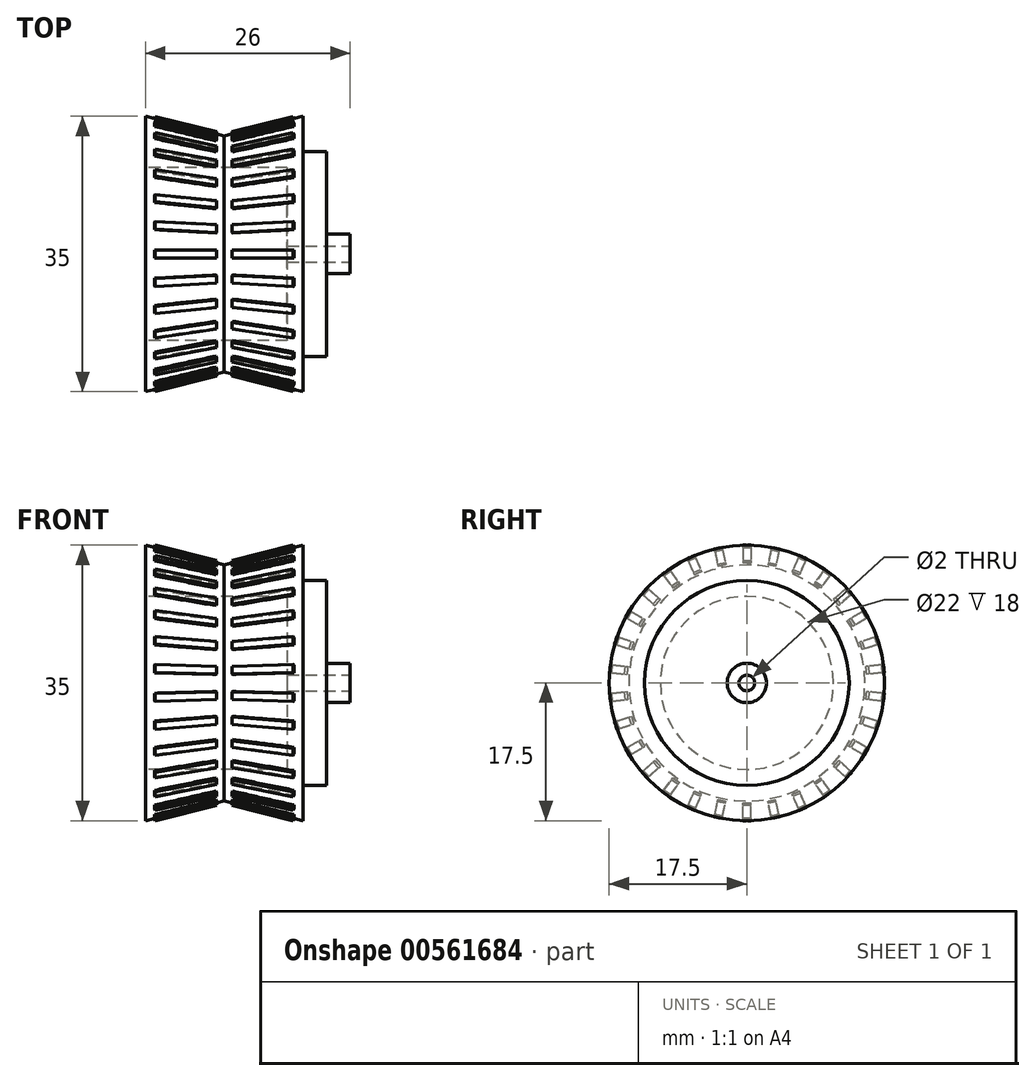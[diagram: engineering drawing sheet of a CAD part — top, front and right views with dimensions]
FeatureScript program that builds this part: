
annotation { "Feature Type Name" : "Feature", "Feature Type Description" : "" }
export const myFeature = defineFeature(function(context is Context, id is Id, definition is map)
    precondition{}
    {
        {
            var Q0;
            Q0=qCreatedBy(makeId("Front.planeOp"),FACE);
            var sketch = newSketch(context, id + "F0", { "sketchPlane" : qUnion([Q0])});
            skLineSegment(sketch, "E0", {"start": v(0, 15) * mm, "end": v(0, -15) * mm, "construction": true});
            skLineSegment(sketch, "E1", {"start": v(0, 15) * mm, "end": v(10, 17.5) * mm});
            skLineSegment(sketch, "E2", {"start": v(10, 17.5) * mm, "end": v(10, 0) * mm});
            skLineSegment(sketch, "E3", {"start": v(-10, 0) * mm, "end": v(-10, 17.5) * mm});
            skLineSegment(sketch, "E4", {"start": v(-10, 17.5) * mm, "end": v(0, 15) * mm});
            skLineSegment(sketch, "E5", {"start": v(-10, 0) * mm, "end": v(10, 0) * mm});
            skPoint(sketch, "E6.orphan", {"position": v(10, -17.5) * mm});
            skPoint(sketch, "E7.orphan", {"position": v(-10, -17.5) * mm});
            skSolve(sketch);
        }
        {
            var Q0;
            Q0=makeQuery(id+"F0.imprint","IMPRINT",FACE,{"disambiguationData":[TD([[makeQuery(id+"F0.imprint","IMPRINT",EDGE,{"derivedFrom":sQuery(id+"F0.wireOp",EDGE,"E1")}),-1.0]])]});
            var Q1;
            Q1=sQuery(id+"F0.wireOp",EDGE,"E5");
            revolve(context, id + "F1", {"entities" : qUnion([Q0]), "axis" : qUnion([Q1]), "revolveType" : RevolveType.FULL});
        }
        {
            var Q0;
            Q0=makeQuery(id+"F1.opRevolve","SWEPT_FACE",FACE,{"disambiguationData":[OSD([sQuery(id+"F0.wireOp",EDGE,"E2")])]});
            var sketch = newSketch(context, id + "F2", { "sketchPlane" : qUnion([Q0])});
            skCircle(sketch, "E8", {"center": v(0, 0) * mm, "radius": 13 * mm});
            skSolve(sketch);
        }
        {
            var Q0;
            Q0=makeQuery(id+"F2.imprint","IMPRINT",FACE,{"disambiguationData":[TD([[makeQuery(id+"F2.imprint","IMPRINT",EDGE,{"derivedFrom":sQuery(id+"F2.wireOp",EDGE,"E8")}),1.0]])]});
            extrude(context, id + "F3", {"entities" : qUnion([Q0]), "operationType" : NewBodyOperationType.ADD, "depth" : 3 * mm, "offsetDistance" : 25 * mm});
        }
        {
            var Q0;
            Q0=makeQuery(id+"F3.opExtrude","CAP_FACE",FACE,{"disambiguationData":[OSD([sQuery(id+"F2.wireOp",EDGE,"E8")])],"isStart":false});
            var sketch = newSketch(context, id + "F4", { "sketchPlane" : qUnion([Q0])});
            skCircle(sketch, "E9", {"center": v(0, 0) * mm, "radius": 2.5 * mm});
            skSolve(sketch);
        }
        {
            var Q0;
            Q0=makeQuery(id+"F4.imprint","IMPRINT",FACE,{"disambiguationData":[TD([[makeQuery(id+"F4.imprint","IMPRINT",EDGE,{"derivedFrom":sQuery(id+"F4.wireOp",EDGE,"E9")}),1.0]])]});
            extrude(context, id + "F5", {"entities" : qUnion([Q0]), "operationType" : NewBodyOperationType.ADD, "depth" : 3 * mm, "offsetDistance" : 25 * mm});
        }
        {
            var Q0;
            Q0=makeQuery(id+"F5.opExtrude","CAP_FACE",FACE,{"disambiguationData":[OSD([sQuery(id+"F4.wireOp",EDGE,"E9")])],"isStart":false});
            var sketch = newSketch(context, id + "F6", { "sketchPlane" : qUnion([Q0])});
            skPoint(sketch, "E10", {"position": v(0, 0) * mm});
            skSolve(sketch);
        }
        {
            var Q0;
            Q0=sQuery(id+"F6.wireOp",VERTEX,"E10");
            var Q1;
            Q1=makeQuery(id+"F1.opRevolve","SWEPT_BODY",BODY,{"disambiguationData":[OSD([sQuery(id+"F0.wireOp",EDGE,"E1"),sQuery(id+"F0.wireOp",EDGE,"E2"),sQuery(id+"F0.wireOp",EDGE,"E3"),sQuery(id+"F0.wireOp",EDGE,"E4"),sQuery(id+"F0.wireOp",EDGE,"E5")])]});
            hole(context, id + "F7", {"style" : HoleStyle.SIMPLE, "endStyle" : HoleEndStyle.THROUGH, "holeDiameter" : 2 * mm, "isTappedThrough" : true, "tappedDepth" : 12 * mm, "tapClearance" : 3, "locations" : qUnion([Q0]), "scope" : qUnion([Q1])});
        }
        {
            var Q0;
            Q0=makeQuery(id+"F1.opRevolve","SWEPT_FACE",FACE,{"disambiguationData":[OSD([sQuery(id+"F0.wireOp",EDGE,"E3")])]});
            var sketch = newSketch(context, id + "F8", { "sketchPlane" : qUnion([Q0])});
            skCircle(sketch, "E11", {"center": v(0, 0) * mm, "radius": 11 * mm});
            skSolve(sketch);
        }
        {
            var Q0;
            Q0=makeQuery(id+"F8.imprint","IMPRINT",FACE,{"disambiguationData":[TD([[makeQuery(id+"F8.imprint","IMPRINT",EDGE,{"derivedFrom":sQuery(id+"F8.wireOp",EDGE,"E11")}),1.0]])]});
            extrude(context, id + "F9", {"entities" : qUnion([Q0]), "operationType" : NewBodyOperationType.REMOVE, "oppositeDirection" : true, "depth" : 18 * mm, "offsetDistance" : 25 * mm});
        }
        {
            var Q0;
            Q0=qCreatedBy(makeId("Front.planeOp"),FACE);
            var sketch = newSketch(context, id + "F10", { "sketchPlane" : qUnion([Q0])});
            skLineSegment(sketch, "E12", {"start": v(-10, 17.5) * mm, "end": v(0, 15) * mm, "construction": true});
            skLineSegment(sketch, "E13", {"start": v(0, -15) * mm, "end": v(-10, -17.5) * mm});
            skLineSegment(sketch, "E14", {"start": v(10, -17.5) * mm, "end": v(0, -15) * mm});
            skLineSegment(sketch, "E15", {"start": v(0, 15) * mm, "end": v(10, 17.5) * mm, "construction": true});
            skLineSegment(sketch, "E16", {"start": v(-9, 16.53) * mm, "end": v(-8.76, 17.5) * mm});
            skLineSegment(sketch, "E17", {"start": v(-8.76, 17.5) * mm, "end": v(-1, 15.56) * mm});
            skLineSegment(sketch, "E18", {"start": v(-1, 15.56) * mm, "end": v(-1.24, 14.59) * mm});
            skLineSegment(sketch, "E19", {"start": v(-1.24, 14.59) * mm, "end": v(-9, 16.53) * mm});
            skLineSegment(sketch, "E20.MirrorCS", {"start": v(9, 16.53) * mm, "end": v(8.76, 17.5) * mm});
            skLineSegment(sketch, "E21.MirrorCS", {"start": v(1.24, 14.59) * mm, "end": v(9, 16.53) * mm});
            skLineSegment(sketch, "E22.MirrorCS", {"start": v(1, 15.56) * mm, "end": v(1.24, 14.59) * mm});
            skLineSegment(sketch, "E23.MirrorCS", {"start": v(8.76, 17.5) * mm, "end": v(1, 15.56) * mm});
            skSolve(sketch);
        }
        {
            var Q0;
            Q0=makeQuery(id+"F10.imprint","IMPRINT",FACE,{"disambiguationData":[TD([[makeQuery(id+"F10.imprint","IMPRINT",EDGE,{"derivedFrom":sQuery(id+"F10.wireOp",EDGE,"E16")}),-1.0]])]});
            var Q1;
            Q1=makeQuery(id+"F10.imprint","IMPRINT",FACE,{"disambiguationData":[TD([[makeQuery(id+"F10.imprint","IMPRINT",EDGE,{"derivedFrom":sQuery(id+"F10.wireOp",EDGE,"E20.MirrorCS")}),1.0]])]});
            extrude(context, id + "F11", {"entities" : qUnion([Q0, Q1]), "operationType" : NewBodyOperationType.ADD, "endBound" : BoundingType.SYMMETRIC, "depth" : 1 * mm, "offsetDistance" : 25 * mm});
        }
        {
            var Q0;
            Q0=makeQuery(id+"F1.opRevolve","SWEPT_BODY",BODY,{"disambiguationData":[OSD([sQuery(id+"F0.wireOp",EDGE,"E1"),sQuery(id+"F0.wireOp",EDGE,"E2"),sQuery(id+"F0.wireOp",EDGE,"E3"),sQuery(id+"F0.wireOp",EDGE,"E4"),sQuery(id+"F0.wireOp",EDGE,"E5")])]});
            var Q1;
            Q1=makeQuery(id+"F5.opExtrude","SWEPT_FACE",FACE,{"disambiguationData":[OSD([sQuery(id+"F4.wireOp",EDGE,"E9")])]});
            circularPattern(context, id + "F12", {"operationType" : NewBodyOperationType.ADD, "entities" : qUnion([Q0]), "axis" : qUnion([Q1]), "angle" : 360 * degree, "instanceCount" : 30, "equalSpace" : true});
        }
    });
